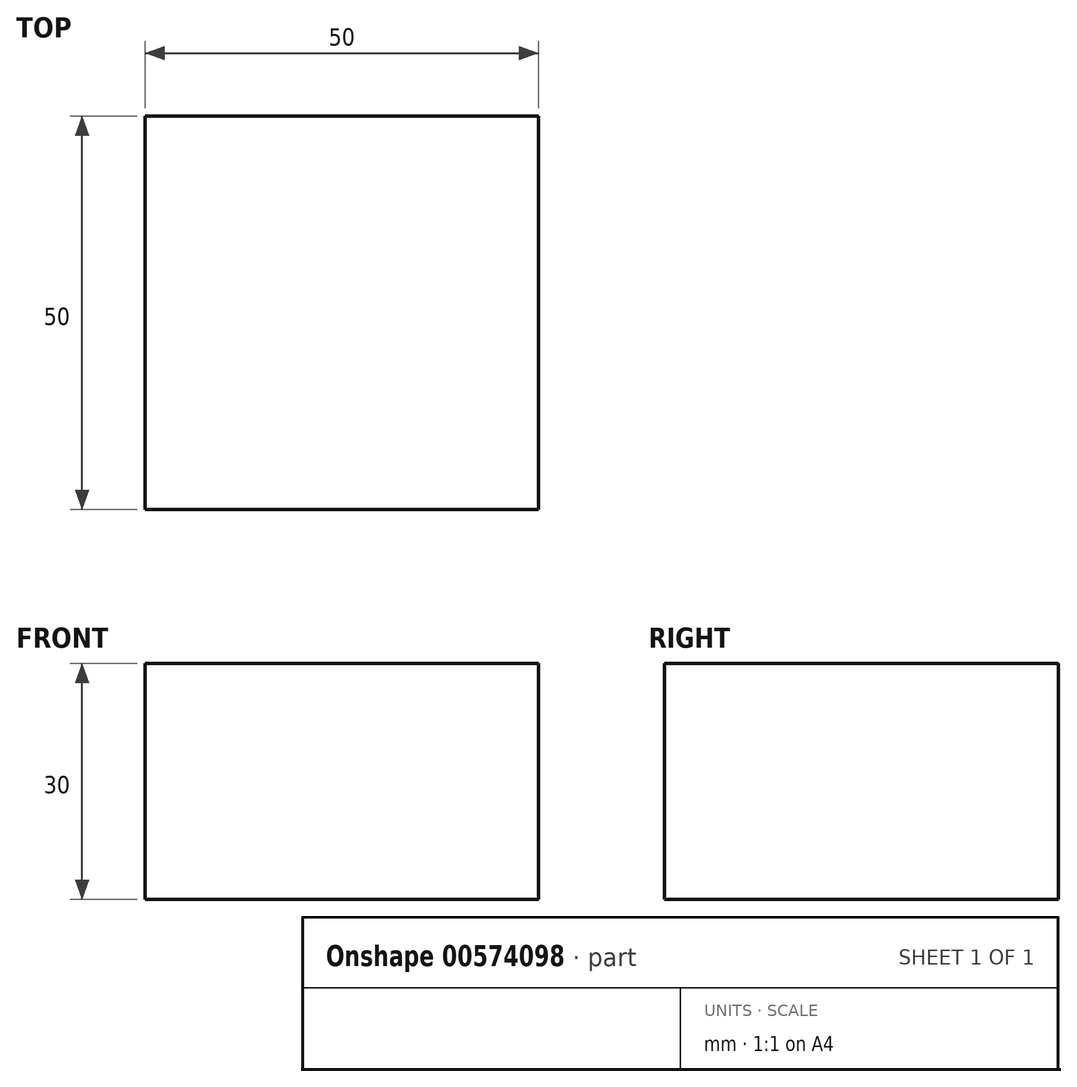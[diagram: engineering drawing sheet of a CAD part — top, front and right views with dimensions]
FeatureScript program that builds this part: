
annotation { "Feature Type Name" : "Feature", "Feature Type Description" : "" }
export const myFeature = defineFeature(function(context is Context, id is Id, definition is map)
    precondition{}
    {
        {
            var Q0;
            Q0=qCreatedBy(makeId("Top.planeOp"),FACE);
            var sketch = newSketch(context, id + "F0", { "sketchPlane" : qUnion([Q0])});
            skLineSegment(sketch, "E0.bottom", {"start": v(-26.45, 26) * mm, "end": v(23.55, 26) * mm});
            skLineSegment(sketch, "E0.top", {"start": v(-26.45, -24) * mm, "end": v(23.55, -24) * mm});
            skLineSegment(sketch, "E0.left", {"start": v(-26.45, 26) * mm, "end": v(-26.45, -24) * mm});
            skLineSegment(sketch, "E0.right", {"start": v(23.55, 26) * mm, "end": v(23.55, -24) * mm});
            skSolve(sketch);
        }
        {
            var Q0;
            Q0=makeQuery(id+"F0.imprint","IMPRINT",FACE,{"disambiguationData":[TD([[makeQuery(id+"F0.imprint","IMPRINT",EDGE,{"derivedFrom":sQuery(id+"F0.wireOp",EDGE,"E0.bottom")}),-1.0]])]});
            extrude(context, id + "F1", {"entities" : qUnion([Q0]), "depth" : 30 * mm, "offsetDistance" : 25 * mm});
        }
    });
